# Revit family: Sink_Top_Mount-American_Standard-Colony-22SB.625228XS.075
name_source: partatom
category: Plumbing Fixtures
units: mm (PartAtom-declared; Revit-internal decimal feet)

## family parameters
Always vertical = No
Cut with Voids When Loaded = Yes
OmniClass Number = 23.45.05.14.14
OmniClass Title = Sinks/Lavatories
Part Type = Normal
Room Calculation Point = No
Round Connector Dimension = Use Diameter
Shared = Yes
Work Plane-Based = Yes

## types (2) — shared parameters
ADA Compliant = Yes
Assembly Code = D2010410
Basin Shape = Rectangular
CW Connection = Yes
CWFU = 1.5
Cold Water Connection Diameter = 1/2"
Cold Water Connection Radius = 1/4"
Cold Water Connection Width = 4"
Default Elevation = 0"
Finish = Stainless Steel-American Standard-075-Brushed
HW Connection = Yes
HWFU = 1.5
Height = 6"
Hot Water Connection Diameter = 1"
Hot Water Connection Radius = 1/4"
Hot Water Connection Width = 4"
Installation Instruction Link = https://lixil.cdn.celum.cloud
Installation Type = Top Mount
Length = 25"
Manufacturer = American Standard
Material = Stainless Steel-American Standard-075-Satin
Price = Prices may vary. Please consult Manufacturer Representative for most up-to-date price list.
Product Documentation Link = https://lixil.cdn.celum.cloud
Product Page URL = https://www.americanstandard-us.com
Revised Date = 11/04/2024
URL = https://www.americanstandard-us.com
Vent Connection = No
WFU = 2
Wall Distance = 1 1/2"
Warranty Information = Limited Lifetime Warranty
Waste Connection = Yes
Waste Connection Diameter = 1 1/2"
Waste Connection Radius = 3/4"
Width = 22 1/16"

## per-type parameters (varying)
| type | Description | Far Right Faucet Hole | Hole Location |
| 22SB.6252283S.075 | Colony® 25 x 22-Inch Stainless Steel 3-Hole Top Mount Single-Bowl ADA Kitchen Sink | No | 25" |
| 22SB.6332284S.075 | Colony® 25 x 22-Inch Stainless Steel 4-Hole Top Mount Single-Bowl ADA Kitchen Sink | Yes | 8" |

note: column(s) folded — value = type name in every type: Model

## geometry (parser evidence)
native form markers: Sweep x2
no freeform markers — native parametric forms only
